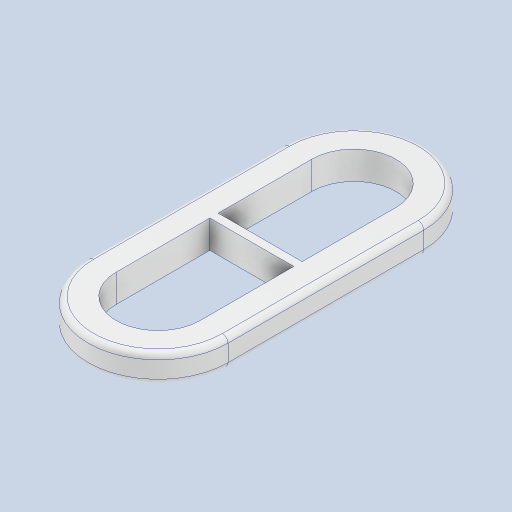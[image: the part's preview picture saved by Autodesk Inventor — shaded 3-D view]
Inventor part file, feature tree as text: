
AUTODESK INVENTOR PART (.ipt)
format: ipt  version: 2024 (Build 280153000, 153)  size: 179,712 bytes
history: native  units: mm
features: extrude x1, fillet x1, sketch x1
ambient origin geometry x8: Origin, YZ Plane, XZ Plane, XY Plane, X Axis, Y Axis, Z Axis, Center Point
bodies: Body1 (feature_tree)
feature tree (3):
  extrude  "Extrusión2"  Depth=10.0mm
  fillet  "Empalme1"  Radius=0.0mm
  sketch  "Boceto1"  dims[d1=50.0mm d3=10.0mm d6=0.0mm d9=1.5mm d10=10.0mm d11=0.0mm d12=2.0mm]
